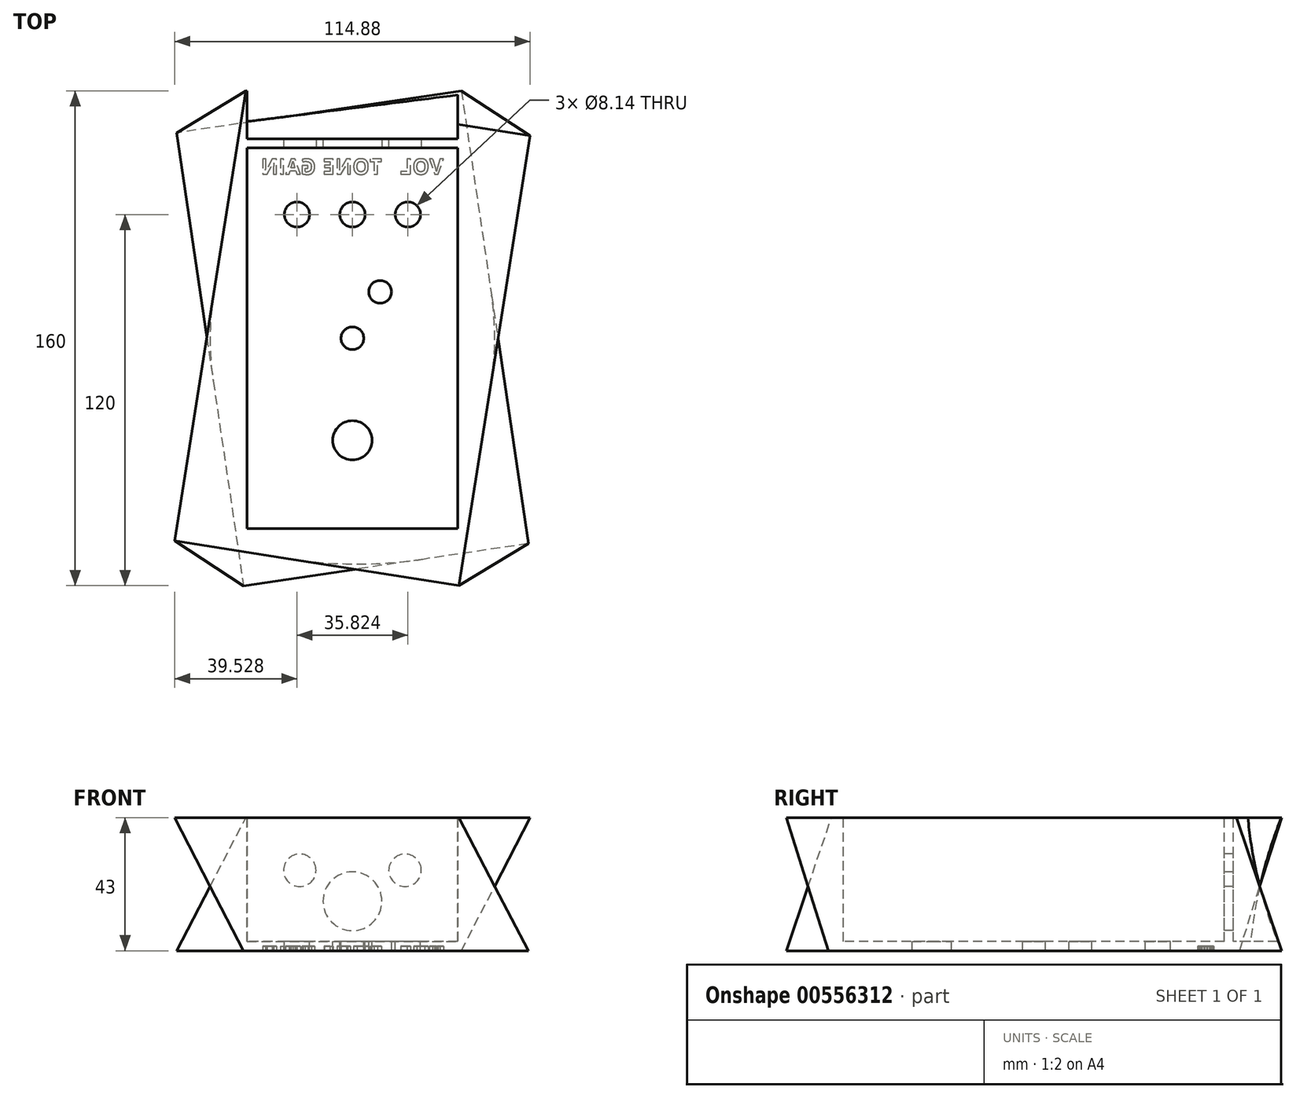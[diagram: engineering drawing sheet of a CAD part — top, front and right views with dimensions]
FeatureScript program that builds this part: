
annotation { "Feature Type Name" : "Feature", "Feature Type Description" : "" }
export const myFeature = defineFeature(function(context is Context, id is Id, definition is map)
    precondition{}
    {
        {
            var Q0;
            Q0=qCreatedBy(makeId("Top.planeOp"),FACE);
            var sketch = newSketch(context, id + "F0", { "sketchPlane" : qUnion([Q0])});
            skLineSegment(sketch, "E0.bottom", {"start": v(-36.5, 64) * mm, "end": v(36.5, 64) * mm});
            skLineSegment(sketch, "E0.top", {"start": v(-36.5, -64) * mm, "end": v(36.5, -64) * mm});
            skLineSegment(sketch, "E0.left", {"start": v(-36.5, 64) * mm, "end": v(-36.5, -64) * mm});
            skLineSegment(sketch, "E0.right", {"start": v(36.5, 64) * mm, "end": v(36.5, -64) * mm});
            skSolve(sketch);
        }
        {
            var Q0;
            Q0=makeQuery(id+"F0.imprint","IMPRINT",FACE,{"disambiguationData":[TD([[makeQuery(id+"F0.imprint","IMPRINT",EDGE,{"derivedFrom":sQuery(id+"F0.wireOp",EDGE,"E0.bottom")}),-1.0]])]});
            extrude(context, id + "F1", {"entities" : qUnion([Q0]), "depth" : 43 * mm, "offsetDistance" : 25 * mm});
        }
        {
            var Q0;
            {var subQ0=sQuery(id+"F0.wireOp",EDGE,"E0.bottom");var subQ1=sQuery(id+"F0.wireOp",EDGE,"E0.left");var subQ2=sQuery(id+"F0.wireOp",EDGE,"E0.top");var subQ3=sQuery(id+"F0.wireOp",EDGE,"E0.right");Q0=makeQuery(id+"F16.boolean.opBoolean","SPLIT",FACE,{"disambiguationData":[TD([makeQuery(id+"F1.opExtrude","SWEPT_FACE",FACE,{"disambiguationData":[OSD([subQ0])]})])],"derivedFrom":makeQuery(id+"F1.opExtrude","CAP_FACE",FACE,{"disambiguationData":[OSD([subQ0,subQ2,subQ1,subQ3])],"isStart":true})});}
            var sketch = newSketch(context, id + "F2", { "sketchPlane" : qUnion([Q0])});
            skLineSegment(sketch, "E1.bottom", {"start": v(35.18, -80) * mm, "end": v(-56.82, -66.4) * mm});
            skLineSegment(sketch, "E1.top", {"start": v(56.82, 66.4) * mm, "end": v(-35.18, 80) * mm});
            skLineSegment(sketch, "E1.left", {"start": v(35.18, -80) * mm, "end": v(56.82, 66.4) * mm});
            skLineSegment(sketch, "E1.right", {"start": v(-56.82, -66.4) * mm, "end": v(-35.18, 80) * mm});
            skPoint(sketch, "E1.middle", {"position": v(0, 0) * mm});
            skSolve(sketch);
        }
        {
            var Q0;
            Q0=makeQuery(id+"F1.opExtrude","CAP_FACE",FACE,{"disambiguationData":[OSD([sQuery(id+"F0.wireOp",EDGE,"E0.bottom"),sQuery(id+"F0.wireOp",EDGE,"E0.top"),sQuery(id+"F0.wireOp",EDGE,"E0.left"),sQuery(id+"F0.wireOp",EDGE,"E0.right")])],"isStart":false});
            var sketch = newSketch(context, id + "F3", { "sketchPlane" : qUnion([Q0])});
            skLineSegment(sketch, "E2.bottom", {"start": v(-34.41, 79.99) * mm, "end": v(57.44, 65.44) * mm});
            skLineSegment(sketch, "E2.top", {"start": v(-57.44, -65.44) * mm, "end": v(34.41, -79.99) * mm});
            skLineSegment(sketch, "E2.left", {"start": v(-34.41, 79.99) * mm, "end": v(-57.44, -65.44) * mm});
            skLineSegment(sketch, "E2.right", {"start": v(57.44, 65.44) * mm, "end": v(34.41, -79.99) * mm});
            skPoint(sketch, "E2.middle", {"position": v(0, 0) * mm});
            skSolve(sketch);
        }
        {
            var Q1;
            Q1 = qSketchRegion(id + "F2", true);
            var Q2;
            Q2 = qSketchRegion(id + "F3", true);
            var Q3;
            Q3=sQuery(id+"F2.wireOp",VERTEX,"E1.left.start");
            var Q4;
            Q4=sQuery(id+"F3.wireOp",VERTEX,"E2.right.start");
            loft(context, id + "F4", {"operationType" : NewBodyOperationType.ADD, "sheetProfilesArray" : [{ "sheetProfileEntities" : qUnion([Q1]) }, { "sheetProfileEntities" : qUnion([Q2]) }], "matchConnections" : true, "connections" : [{ "connectionEntities" : qUnion([Q3, Q4]), "connectionEdgeQueries" : qUnion([]), "connectionEdgeParameters" : [] }]});
        }
        {
            var Q0;
            Q0=makeQuery(id+"F1.opExtrude","CAP_FACE",FACE,{"disambiguationData":[OSD([sQuery(id+"F0.wireOp",EDGE,"E0.bottom"),sQuery(id+"F0.wireOp",EDGE,"E0.top"),sQuery(id+"F0.wireOp",EDGE,"E0.left"),sQuery(id+"F0.wireOp",EDGE,"E0.right")])],"isStart":false});
            var sketch = newSketch(context, id + "F5", { "sketchPlane" : qUnion([Q0])});
            skLineSegment(sketch, "E3.bottom", {"start": v(-34, 61.5) * mm, "end": v(34, 61.5) * mm});
            skLineSegment(sketch, "E3.top", {"start": v(-34, -61.5) * mm, "end": v(34, -61.5) * mm});
            skLineSegment(sketch, "E3.left", {"start": v(-34, 61.5) * mm, "end": v(-34, -61.5) * mm});
            skLineSegment(sketch, "E3.right", {"start": v(34, 61.5) * mm, "end": v(34, -61.5) * mm});
            skSolve(sketch);
        }
        {
            var Q0;
            Q0=makeQuery(id+"F5.imprint","IMPRINT",FACE,{"disambiguationData":[TD([[makeQuery(id+"F5.imprint","IMPRINT",EDGE,{"derivedFrom":sQuery(id+"F5.wireOp",EDGE,"E3.bottom")}),-1.0]])]});
            extrude(context, id + "F6", {"entities" : qUnion([Q0]), "operationType" : NewBodyOperationType.REMOVE, "oppositeDirection" : true, "depth" : 40 * mm, "offsetDistance" : 25 * mm});
        }
        {
            var Q0;
            Q0=makeQuery(id+"F6.boolean.opBoolean","COPY",FACE,{"derivedFrom":makeQuery(id+"F6.opExtrude","CAP_FACE",FACE,{"disambiguationData":[OSD([sQuery(id+"F5.wireOp",EDGE,"E3.bottom"),sQuery(id+"F5.wireOp",EDGE,"E3.top"),sQuery(id+"F5.wireOp",EDGE,"E3.left"),sQuery(id+"F5.wireOp",EDGE,"E3.right")])],"isStart":false})});
            var sketch = newSketch(context, id + "F7", { "sketchPlane" : qUnion([Q0])});
            skCircle(sketch, "E4", {"center": v(-17.91, 40) * mm, "radius": 4.07 * mm});
            skCircle(sketch, "E5", {"center": v(0, 40) * mm, "radius": 4.07 * mm});
            skCircle(sketch, "E6", {"center": v(17.91, 40) * mm, "radius": 4.07 * mm});
            skCircle(sketch, "E7", {"center": v(0, -33) * mm, "radius": 6.35 * mm});
            skLineSegment(sketch, "E8", {"start": v(17.91, 40) * mm, "end": v(0, 40) * mm, "construction": true});
            skLineSegment(sketch, "E9", {"start": v(8.96, 40) * mm, "end": v(8.96, 15.16) * mm, "construction": true});
            skCircle(sketch, "E10", {"center": v(8.96, 15) * mm, "radius": 3.67 * mm});
            skCircle(sketch, "E11", {"center": v(0, 0) * mm, "radius": 3.67 * mm});
            skSolve(sketch);
        }
        {
            var Q0;
            Q0=qSketchRegion(id+"F7",true);
            extrude(context, id + "F8", {"entities" : qUnion([Q0]), "operationType" : NewBodyOperationType.REMOVE, "oppositeDirection" : true, "depth" : 25 * mm, "offsetDistance" : 25 * mm});
        }
        {
            var Q0;
            Q0=makeQuery(id+"F6.boolean.opBoolean","COPY",FACE,{"derivedFrom":makeQuery(id+"F6.opExtrude","SWEPT_FACE",FACE,{"disambiguationData":[OSD([sQuery(id+"F5.wireOp",EDGE,"E3.bottom")])]})});
            cPlane(context, id + "F9", {"entities" : qUnion([Q0]), "cplaneType" : CPlaneType.OFFSET, "offset" : 3 * mm, "oppositeDirection" : true, "width" : 150 * mm, "height" : 150 * mm});
        }
        {
            var Q0;
            Q0=qCreatedBy(id+"F9.planeOp",FACE);
            var sketch = newSketch(context, id + "F10", { "sketchPlane" : qUnion([Q0])});
            skCircle(sketch, "E12", {"center": v(0, 16) * mm, "radius": 9.5 * mm});
            skCircle(sketch, "E13", {"center": v(17, 26) * mm, "radius": 5.26 * mm});
            skCircle(sketch, "E14", {"center": v(-17, 26) * mm, "radius": 5.26 * mm});
            skSolve(sketch);
        }
        {
            var Q0;
            Q0=qSketchRegion(id+"F10",true);
            extrude(context, id + "F11", {"entities" : qUnion([Q0]), "operationType" : NewBodyOperationType.REMOVE, "endBound" : BoundingType.SYMMETRIC, "oppositeDirection" : true, "depth" : 30 * mm, "offsetDistance" : 25 * mm});
        }
        {
            var Q0;
            Q0=qCreatedBy(id+"F9.planeOp",FACE);
            var sketch = newSketch(context, id + "F12", { "sketchPlane" : qUnion([Q0])});
            skLineSegment(sketch, "E15.0", {"start": v(-34, 3) * mm, "end": v(-34, 43) * mm});
            skLineSegment(sketch, "E16.0", {"start": v(-34, 3) * mm, "end": v(34, 3) * mm});
            skLineSegment(sketch, "E17.0", {"start": v(34, 3) * mm, "end": v(34, 43) * mm});
            skLineSegment(sketch, "E18.0", {"start": v(-34, 43) * mm, "end": v(34, 43) * mm});
            skSolve(sketch);
        }
        {
            var Q0;
            Q0 = qSketchRegion(id + "F12", true);
            extrude(context, id + "F13", {"entities" : qUnion([Q0]), "operationType" : NewBodyOperationType.REMOVE, "oppositeDirection" : true, "depth" : 25 * mm, "offsetDistance" : 25 * mm});
        }
        {
            var Q0;
            Q0=qCreatedBy(makeId("Front.planeOp"),FACE);
            cPlane(context, id + "F14", {"entities" : qUnion([Q0]), "cplaneType" : CPlaneType.OFFSET, "offset" : 38 * mm, "width" : 150 * mm, "height" : 150 * mm});
        }
        {
            var Q0;
            Q0=makeQuery(id+"F1.opExtrude","CAP_FACE",FACE,{"disambiguationData":[OSD([sQuery(id+"F0.wireOp",EDGE,"E0.bottom"),sQuery(id+"F0.wireOp",EDGE,"E0.top"),sQuery(id+"F0.wireOp",EDGE,"E0.left"),sQuery(id+"F0.wireOp",EDGE,"E0.right")])],"isStart":true});
            var sketch = newSketch(context, id + "F15", { "sketchPlane" : qUnion([Q0])});
            skText(sketch, "E19", { "text": "VOL", "fontName": "OpenSans-Bold.ttf"});
            skText(sketch, "E20", { "text": "TONE", "fontName": "OpenSans-Bold.ttf"});
            skText(sketch, "E21", { "text": "GAIN", "fontName": "OpenSans-Bold.ttf"});
            const initialGuessF15  = {"E19": [0.0294, -0.053, -1, 0, 0.005], "E20": [0.00956, -0.053, -1, 0, 0.005], "E21": [-0.0118, -0.053, -1, 0, 0.005]};
            skSetInitialGuess(sketch, initialGuessF15);
            skSolve(sketch);
        }
        {
            var Q0;
            Q0=qSketchRegion(id+"F15",true);
            extrude(context, id + "F16", {"entities" : qUnion([Q0]), "operationType" : NewBodyOperationType.REMOVE, "oppositeDirection" : true, "depth" : 1.5 * mm, "offsetDistance" : 25 * mm});
        }
    });
